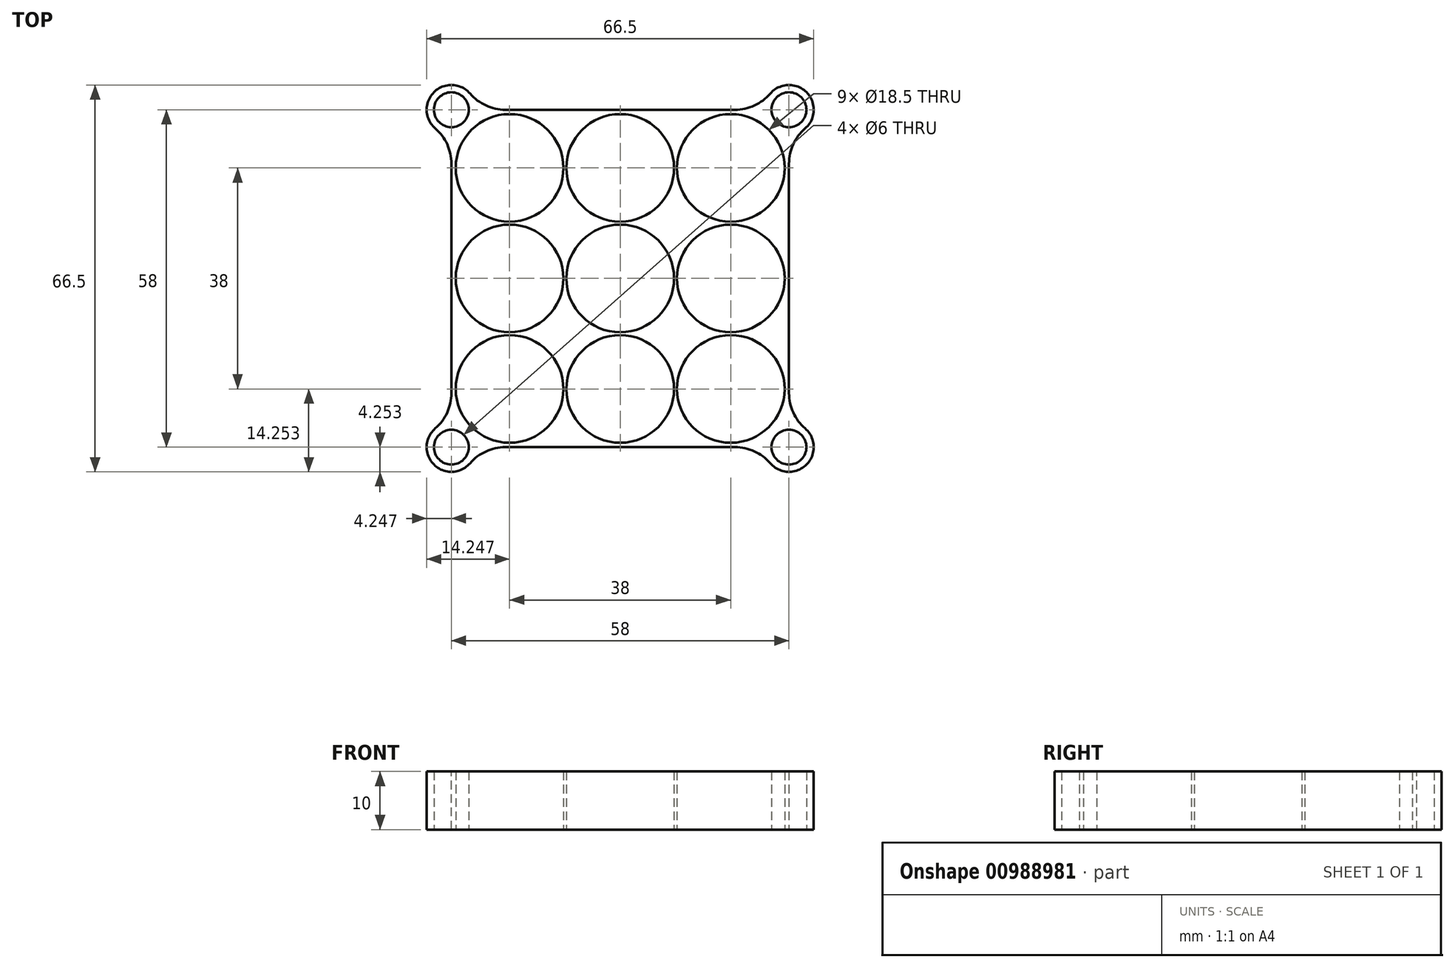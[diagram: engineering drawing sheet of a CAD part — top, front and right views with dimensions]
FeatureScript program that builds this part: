
annotation { "Feature Type Name" : "Feature", "Feature Type Description" : "" }
export const myFeature = defineFeature(function(context is Context, id is Id, definition is map)
    precondition{}
    {
        {
            var Q0;
            Q0=qCreatedBy(makeId("Top.planeOp"),FACE);
            var sketch = newSketch(context, id + "F0", { "sketchPlane" : qUnion([Q0])});
            skCircle(sketch, "E0", {"center": v(-21.4, 11.21) * mm, "radius": 9.25 * mm});
            skCircle(sketch, "E1.0.1.0", {"center": v(-21.4, 30.21) * mm, "radius": 9.25 * mm});
            skCircle(sketch, "E1.0.2.0", {"center": v(-21.4, 49.21) * mm, "radius": 9.25 * mm});
            skCircle(sketch, "E1.1.0.0", {"center": v(-2.4, 11.21) * mm, "radius": 9.25 * mm});
            skCircle(sketch, "E1.1.1.0", {"center": v(-2.4, 30.21) * mm, "radius": 9.25 * mm});
            skCircle(sketch, "E1.1.2.0", {"center": v(-2.4, 49.21) * mm, "radius": 9.25 * mm});
            skCircle(sketch, "E1.2.0.0", {"center": v(16.6, 11.21) * mm, "radius": 9.25 * mm});
            skCircle(sketch, "E1.2.1.0", {"center": v(16.6, 30.21) * mm, "radius": 9.25 * mm});
            skCircle(sketch, "E1.2.2.0", {"center": v(16.6, 49.21) * mm, "radius": 9.25 * mm});
            skLineSegment(sketch, "E1.direction1", {"start": v(-21.4, 11.21) * mm, "end": v(-2.4, 11.21) * mm, "construction": true});
            skLineSegment(sketch, "E1.direction2", {"start": v(-21.4, 11.21) * mm, "end": v(-21.4, 30.21) * mm, "construction": true});
            skLineSegment(sketch, "E2.bottom", {"start": v(26.6, 59.21) * mm, "end": v(-31.4, 59.21) * mm});
            skLineSegment(sketch, "E2.top", {"start": v(26.6, 1.21) * mm, "end": v(-31.4, 1.21) * mm});
            skLineSegment(sketch, "E2.left", {"start": v(26.6, 59.21) * mm, "end": v(26.6, 1.21) * mm});
            skLineSegment(sketch, "E2.right", {"start": v(-31.4, 59.21) * mm, "end": v(-31.4, 1.21) * mm});
            skCircle(sketch, "E3", {"center": v(-31.4, 59.21) * mm, "radius": 4.25 * mm});
            skCircle(sketch, "E4.0", {"center": v(-31.4, 59.21) * mm, "radius": 3 * mm});
            skCircle(sketch, "E5.0.1.0", {"center": v(-31.4, 1.21) * mm, "radius": 3 * mm});
            skCircle(sketch, "E5.0.1.1", {"center": v(-31.4, 1.21) * mm, "radius": 4.25 * mm});
            skCircle(sketch, "E5.1.0.0", {"center": v(26.6, 59.21) * mm, "radius": 3 * mm});
            skCircle(sketch, "E5.1.0.1", {"center": v(26.6, 59.21) * mm, "radius": 4.25 * mm});
            skCircle(sketch, "E5.1.1.0", {"center": v(26.6, 1.21) * mm, "radius": 3 * mm});
            skCircle(sketch, "E5.1.1.1", {"center": v(26.6, 1.21) * mm, "radius": 4.25 * mm});
            skLineSegment(sketch, "E5.direction1", {"start": v(-31.4, 59.21) * mm, "end": v(26.6, 59.21) * mm, "construction": true});
            skLineSegment(sketch, "E5.direction2", {"start": v(-31.4, 1.21) * mm, "end": v(-31.4, 59.21) * mm, "construction": true});
            skSolve(sketch);
        }
        {
            var Q0;
            Q0=makeQuery(id+"F0.imprint","IMPRINT",FACE,{"disambiguationData":[TD([[makeQuery(id+"F0.imprint","IMPRINT",EDGE,{"derivedFrom":sQuery(id+"F0.wireOp",EDGE,"E0")}),-1.0]])]});
            var Q1;
            {var subQ0=sQuery(id+"F0.wireOp",EDGE,"E3");var subQ1=sQuery(id+"F0.wireOp",EDGE,"E2.bottom");var subQ2=makeQuery(id+"F0.imprint","INTERSECT",VERTEX,{"derivedFrom":[subQ1,subQ0]});Q1=makeQuery(id+"F0.imprint","IMPRINT",FACE,{"disambiguationData":[TD([[makeQuery(id+"F0.imprint","IMPRINT",EDGE,{"disambiguationData":[TD([[subQ2,-1.0]])],"derivedFrom":subQ1}),-1.0]])]});}
            var Q2;
            {var subQ0=sQuery(id+"F0.wireOp",EDGE,"E3");var subQ1=sQuery(id+"F0.wireOp",EDGE,"E2.bottom");var subQ2=makeQuery(id+"F0.imprint","INTERSECT",VERTEX,{"derivedFrom":[subQ1,subQ0]});Q2=makeQuery(id+"F0.imprint","IMPRINT",FACE,{"disambiguationData":[TD([[makeQuery(id+"F0.imprint","IMPRINT",EDGE,{"disambiguationData":[TD([[subQ2,-1.0]])],"derivedFrom":subQ1}),1.0]])]});}
            var Q3;
            {var subQ0=sQuery(id+"F0.wireOp",EDGE,"E5.0.1.1");var subQ1=sQuery(id+"F0.wireOp",EDGE,"E2.top");var subQ2=makeQuery(id+"F0.imprint","INTERSECT",VERTEX,{"derivedFrom":[subQ1,subQ0]});Q3=makeQuery(id+"F0.imprint","IMPRINT",FACE,{"disambiguationData":[TD([[makeQuery(id+"F0.imprint","IMPRINT",EDGE,{"disambiguationData":[TD([[subQ2,-1.0]])],"derivedFrom":subQ1}),-1.0]])]});}
            var Q4;
            {var subQ0=sQuery(id+"F0.wireOp",EDGE,"E5.0.1.1");var subQ1=sQuery(id+"F0.wireOp",EDGE,"E2.top");var subQ2=makeQuery(id+"F0.imprint","INTERSECT",VERTEX,{"derivedFrom":[subQ1,subQ0]});Q4=makeQuery(id+"F0.imprint","IMPRINT",FACE,{"disambiguationData":[TD([[makeQuery(id+"F0.imprint","IMPRINT",EDGE,{"disambiguationData":[TD([[subQ2,-1.0]])],"derivedFrom":subQ1}),1.0]])]});}
            var Q5;
            {var subQ0=sQuery(id+"F0.wireOp",EDGE,"E5.1.1.1");var subQ1=sQuery(id+"F0.wireOp",EDGE,"E2.top");var subQ2=makeQuery(id+"F0.imprint","INTERSECT",VERTEX,{"derivedFrom":[subQ1,subQ0]});Q5=makeQuery(id+"F0.imprint","IMPRINT",FACE,{"disambiguationData":[TD([[makeQuery(id+"F0.imprint","IMPRINT",EDGE,{"disambiguationData":[TD([[subQ2,1.0]])],"derivedFrom":subQ1}),-1.0]])]});}
            var Q6;
            {var subQ0=sQuery(id+"F0.wireOp",EDGE,"E5.1.1.1");var subQ1=sQuery(id+"F0.wireOp",EDGE,"E2.top");var subQ2=makeQuery(id+"F0.imprint","INTERSECT",VERTEX,{"derivedFrom":[subQ1,subQ0]});Q6=makeQuery(id+"F0.imprint","IMPRINT",FACE,{"disambiguationData":[TD([[makeQuery(id+"F0.imprint","IMPRINT",EDGE,{"disambiguationData":[TD([[subQ2,1.0]])],"derivedFrom":subQ1}),1.0]])]});}
            var Q7;
            {var subQ0=sQuery(id+"F0.wireOp",EDGE,"E5.1.0.1");var subQ1=sQuery(id+"F0.wireOp",EDGE,"E2.bottom");var subQ2=makeQuery(id+"F0.imprint","INTERSECT",VERTEX,{"derivedFrom":[subQ1,subQ0]});Q7=makeQuery(id+"F0.imprint","IMPRINT",FACE,{"disambiguationData":[TD([[makeQuery(id+"F0.imprint","IMPRINT",EDGE,{"disambiguationData":[TD([[subQ2,1.0]])],"derivedFrom":subQ1}),1.0]])]});}
            var Q8;
            {var subQ0=sQuery(id+"F0.wireOp",EDGE,"E5.1.0.1");var subQ1=sQuery(id+"F0.wireOp",EDGE,"E2.bottom");var subQ2=makeQuery(id+"F0.imprint","INTERSECT",VERTEX,{"derivedFrom":[subQ1,subQ0]});Q8=makeQuery(id+"F0.imprint","IMPRINT",FACE,{"disambiguationData":[TD([[makeQuery(id+"F0.imprint","IMPRINT",EDGE,{"disambiguationData":[TD([[subQ2,1.0]])],"derivedFrom":subQ1}),-1.0]])]});}
            extrude(context, id + "F1", {"entities" : qUnion([Q0, Q1, Q2, Q3, Q4, Q5, Q6, Q7, Q8]), "depth" : 10 * mm, "offsetDistance" : 25 * mm});
        }
        {
            var Q0;
            Q0=makeQuery(id+"F1.opExtrude","SWEPT_EDGE",EDGE,{"disambiguationData":[OSD([sQuery(id+"F0.wireOp",EDGE,"E2.left"),sQuery(id+"F0.wireOp",EDGE,"E5.1.0.1")])]});
            var Q1;
            Q1=makeQuery(id+"F1.opExtrude","SWEPT_EDGE",EDGE,{"disambiguationData":[OSD([sQuery(id+"F0.wireOp",EDGE,"E2.bottom"),sQuery(id+"F0.wireOp",EDGE,"E5.1.0.1")])]});
            var Q2;
            Q2=makeQuery(id+"F1.opExtrude","SWEPT_EDGE",EDGE,{"disambiguationData":[OSD([sQuery(id+"F0.wireOp",EDGE,"E2.bottom"),sQuery(id+"F0.wireOp",EDGE,"E3")])]});
            var Q3;
            Q3=makeQuery(id+"F1.opExtrude","SWEPT_EDGE",EDGE,{"disambiguationData":[OSD([sQuery(id+"F0.wireOp",EDGE,"E2.top"),sQuery(id+"F0.wireOp",EDGE,"E5.0.1.1")])]});
            var Q4;
            Q4=makeQuery(id+"F1.opExtrude","SWEPT_EDGE",EDGE,{"disambiguationData":[OSD([sQuery(id+"F0.wireOp",EDGE,"E2.right"),sQuery(id+"F0.wireOp",EDGE,"E5.0.1.1")])]});
            var Q5;
            Q5=makeQuery(id+"F1.opExtrude","SWEPT_EDGE",EDGE,{"disambiguationData":[OSD([sQuery(id+"F0.wireOp",EDGE,"E2.right"),sQuery(id+"F0.wireOp",EDGE,"E3")])]});
            var Q6;
            Q6=makeQuery(id+"F1.opExtrude","SWEPT_EDGE",EDGE,{"disambiguationData":[OSD([sQuery(id+"F0.wireOp",EDGE,"E2.top"),sQuery(id+"F0.wireOp",EDGE,"E5.1.1.1")])]});
            var Q7;
            Q7=makeQuery(id+"F1.opExtrude","SWEPT_EDGE",EDGE,{"disambiguationData":[OSD([sQuery(id+"F0.wireOp",EDGE,"E2.left"),sQuery(id+"F0.wireOp",EDGE,"E5.1.1.1")])]});
            fillet(context, id + "F2", {"entities" : qUnion([Q0, Q1, Q2, Q3, Q4, Q5, Q6, Q7]), "radius" : 8 * mm, "tangentPropagation" : true, "allowEdgeOverflow" : false});
        }
    });
